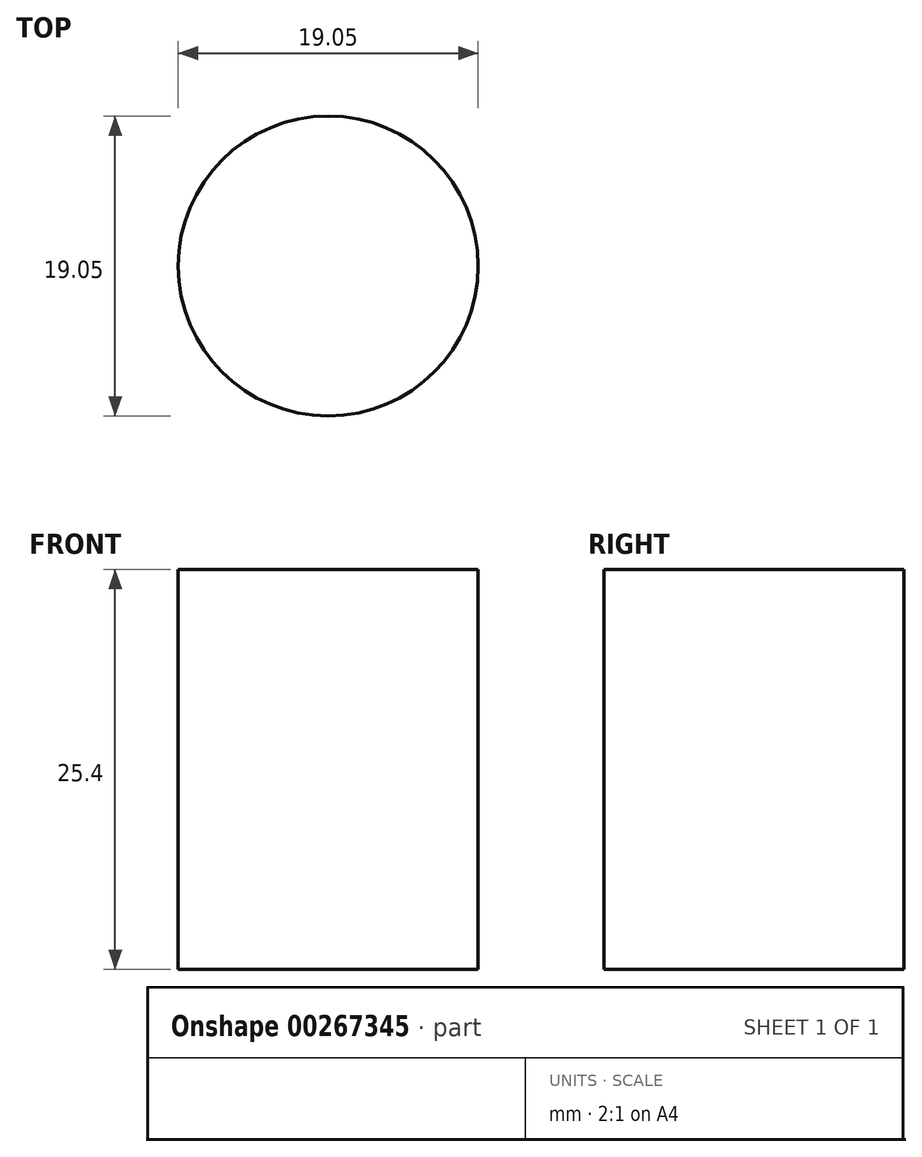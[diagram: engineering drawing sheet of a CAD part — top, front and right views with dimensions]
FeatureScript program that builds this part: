
annotation { "Feature Type Name" : "Feature", "Feature Type Description" : "" }
export const myFeature = defineFeature(function(context is Context, id is Id, definition is map)
    precondition{}
    {
        {
            var Q0;
            Q0=qCreatedBy(makeId("Top.planeOp"),FACE);
            var sketch = newSketch(context, id + "F0", { "sketchPlane" : qUnion([Q0])});
            skCircle(sketch, "E0", {"center": v(-50.31, -37.81) * mm, "radius": 9.53 * mm});
            skSolve(sketch);
        }
        {
            var Q0;
            Q0 = qSketchRegion(id + "F0", true);
            extrude(context, id + "F1", {"entities" : qUnion([Q0]), "depth" : 25.4 * mm});
        }
    });
